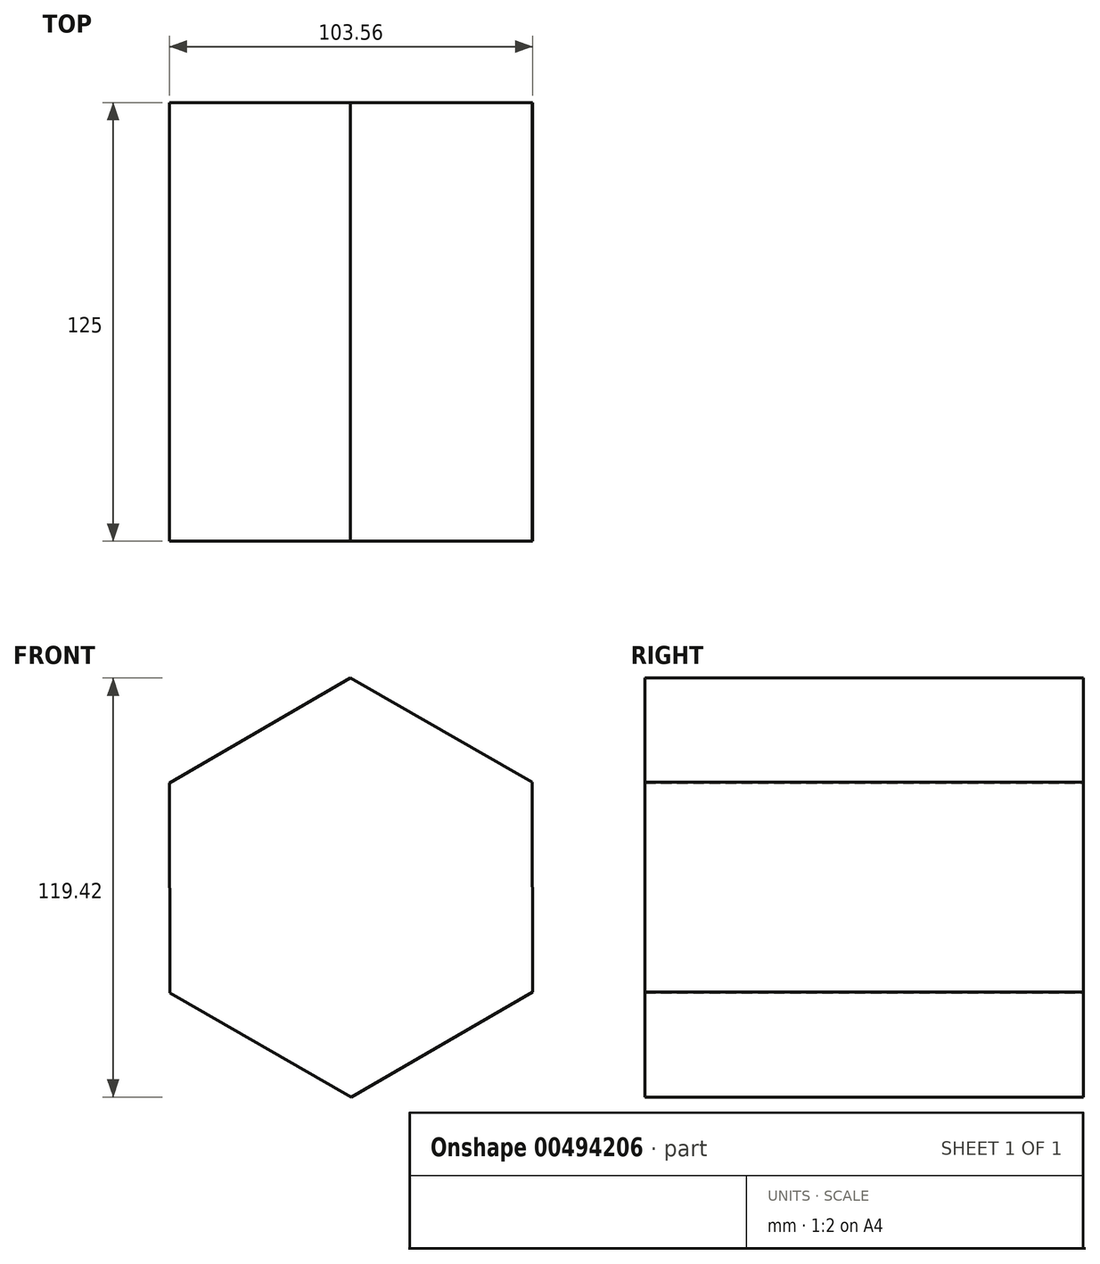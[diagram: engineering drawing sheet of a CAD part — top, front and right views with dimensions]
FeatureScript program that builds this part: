
annotation { "Feature Type Name" : "Feature", "Feature Type Description" : "" }
export const myFeature = defineFeature(function(context is Context, id is Id, definition is map)
    precondition{}
    {
        {
            var Q0;
            Q0=qCreatedBy(makeId("Front.planeOp"),FACE);
            var sketch = newSketch(context, id + "F0", { "sketchPlane" : qUnion([Q0])});
            skCircle(sketch, "E0.cCircle", {"center": v(0, 0) * mm, "radius": 59.71 * mm, "construction": true});
            skLineSegment(sketch, "E0.0", {"start": v(51.64, 29.98) * mm, "end": v(51.78, -29.73) * mm});
            skLineSegment(sketch, "E0.1", {"start": v(51.78, -29.73) * mm, "end": v(0.14, -59.71) * mm});
            skLineSegment(sketch, "E0.2", {"start": v(0.14, -59.71) * mm, "end": v(-51.64, -29.98) * mm});
            skLineSegment(sketch, "E0.3", {"start": v(-51.64, -29.98) * mm, "end": v(-51.78, 29.73) * mm});
            skLineSegment(sketch, "E0.4", {"start": v(-51.78, 29.73) * mm, "end": v(-0.14, 59.71) * mm});
            skLineSegment(sketch, "E0.5", {"start": v(-0.14, 59.71) * mm, "end": v(51.64, 29.98) * mm});
            skSolve(sketch);
        }
        {
            var Q0;
            Q0=makeQuery(id+"F0.imprint","IMPRINT",FACE,{"disambiguationData":[TD([[makeQuery(id+"F0.imprint","IMPRINT",EDGE,{"derivedFrom":sQuery(id+"F0.wireOp",EDGE,"E0.0")}),-1.0]])]});
            extrude(context, id + "F1", {"entities" : qUnion([Q0]), "depth" : 125 * mm});
        }
    });
